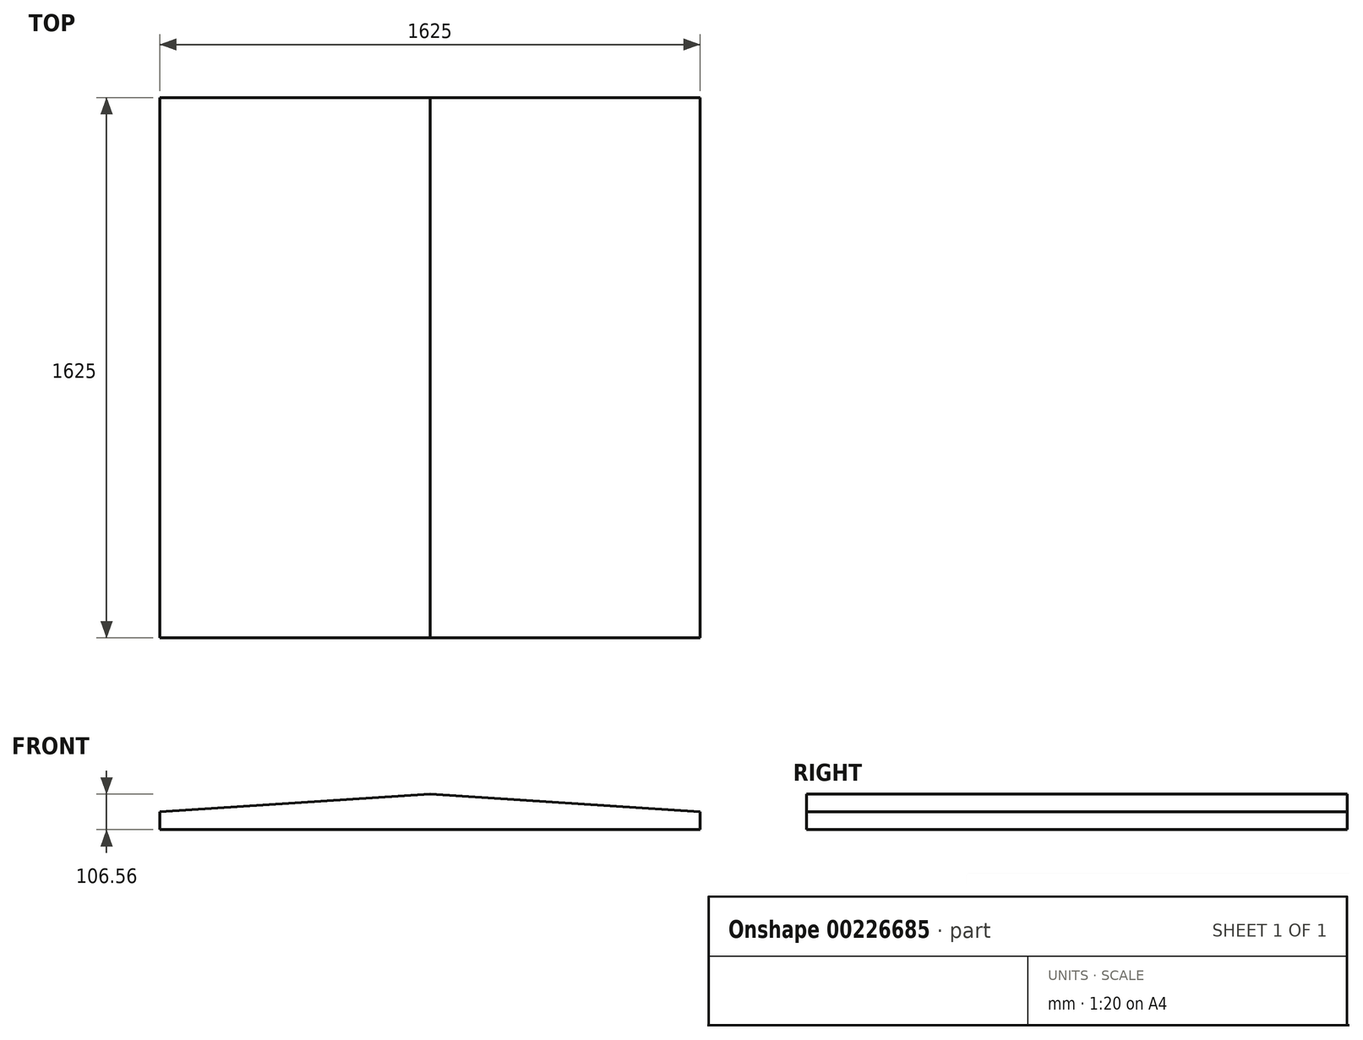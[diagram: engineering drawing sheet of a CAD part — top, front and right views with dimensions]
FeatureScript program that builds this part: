
annotation { "Feature Type Name" : "Feature", "Feature Type Description" : "" }
export const myFeature = defineFeature(function(context is Context, id is Id, definition is map)
    precondition{}
    {
        {
            var Q0;
            Q0=qCreatedBy(makeId("Front.planeOp"),FACE);
            var sketch = newSketch(context, id + "F0", { "sketchPlane" : qUnion([Q0])});
            skLineSegment(sketch, "E0.bottom", {"start": v(812.5, -53.28) * mm, "end": v(-812.5, -53.28) * mm});
            skLineSegment(sketch, "E0.left", {"start": v(812.5, -53.28) * mm, "end": v(812.5, 0) * mm});
            skLineSegment(sketch, "E0.right", {"start": v(-812.5, -53.28) * mm, "end": v(-812.5, 0) * mm});
            skPoint(sketch, "E0.middle", {"position": v(0, 0) * mm});
            skLineSegment(sketch, "E1", {"start": v(-812.5, 0) * mm, "end": v(0, 53.28) * mm});
            skLineSegment(sketch, "E2", {"start": v(0, 53.28) * mm, "end": v(812.5, 0) * mm});
            skPoint(sketch, "E3.orphan", {"position": v(-812.5, 53.28) * mm});
            skPoint(sketch, "E4.orphan", {"position": v(812.5, 53.28) * mm});
            skSolve(sketch);
        }
        {
            var Q0;
            Q0=makeQuery(id+"F0.imprint","IMPRINT",FACE,{"disambiguationData":[TD([[makeQuery(id+"F0.imprint","IMPRINT",EDGE,{"derivedFrom":sQuery(id+"F0.wireOp",EDGE,"E0.bottom")}),-1.0]])]});
            extrude(context, id + "F1", {"entities" : qUnion([Q0]), "depth" : 1625 * mm});
        }
    });
